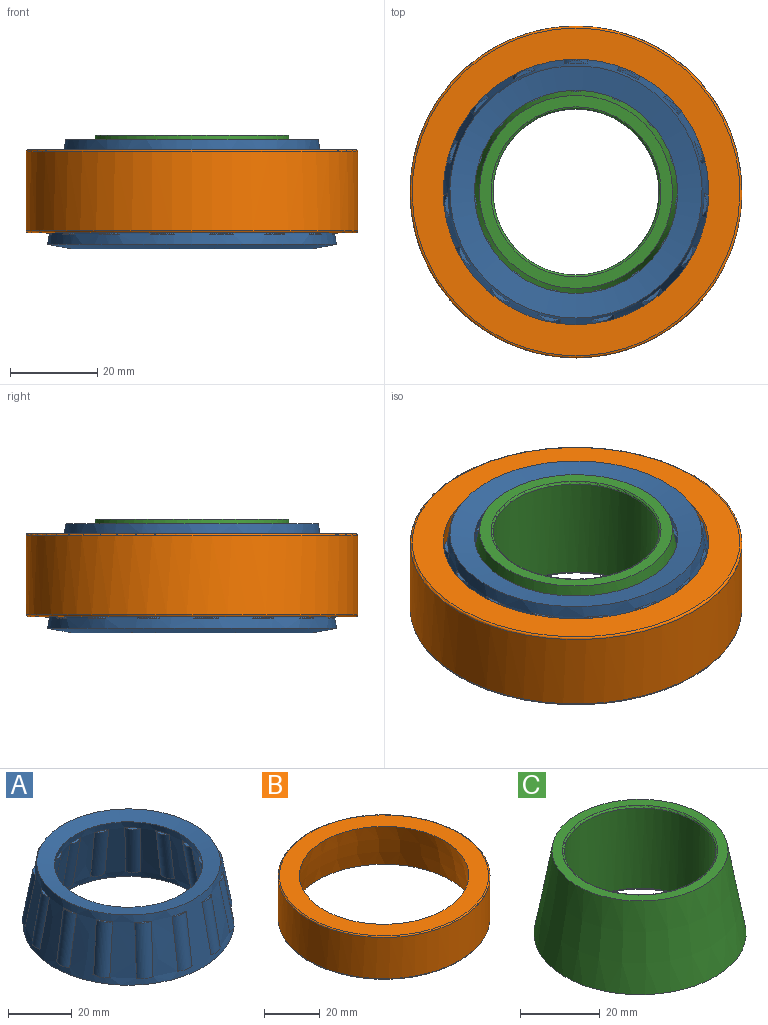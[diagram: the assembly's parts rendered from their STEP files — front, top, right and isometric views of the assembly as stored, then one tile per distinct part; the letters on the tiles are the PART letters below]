
ASSEMBLY  parts=3 mates=3
PART A: 169 faces, bbox 66.9x66.8x25.1 mm
  f0: plane 4.3x1.24mm, normal (0.04,0.17,0.98), area 2.5mm2, adj f2,f123
  f1: plane 4.33x1.25mm, normal (-0.04,-0.17,-0.98), area 2.5mm2, adj f2,f123
  f2: cylinder r=3.69mm len=20.33mm, axis (0.04,0.17,0.98), area 448.5mm2, adj f0,f1,f3,f4,f5,f6,f7,f148
  f3: plane 4.79x1.48mm, normal (0.04,0.17,0.98), area 2.8mm2, adj f2,f122
  f4: plane 4.76x1.47mm, normal (-0.04,-0.17,-0.98), area 2.8mm2, adj f2,f122
  f5: plane 5.52x2.27mm, normal (-0.04,-0.17,-0.98), area 0.8mm2, adj f2,f122,f123,f150
  f6: plane 5.52x2.25mm, normal (0.04,0.17,0.98), area 0.8mm2, adj f2,f122,f123,f150
  f7: plane 5.59x2mm, normal (0.04,0.17,0.98), area 0.8mm2, adj f2,f122,f123,f149
  f8: plane 3.56x2.59mm, normal (0.1,0.14,0.98), area 2.5mm2, adj f10,f123
  f9: plane 3.58x2.6mm, normal (-0.1,-0.14,-0.98), area 2.5mm2, adj f10,f123
  f10: cylinder r=3.69mm len=20.33mm, axis (0.1,0.14,0.98), area 448.5mm2, adj f8,f9,f11,f12,f13,f14,f15,f151
  f11: plane 3.96x2.89mm, normal (0.1,0.14,0.98), area 2.8mm2, adj f10,f122
  f12: plane 3.94x2.87mm, normal (-0.1,-0.14,-0.98), area 2.8mm2, adj f10,f122
  f13: plane 4.54x3.73mm, normal (-0.1,-0.14,-0.98), area 0.8mm2, adj f10,f122,f123,f153
  f14: plane 4.55x3.71mm, normal (0.1,0.14,0.98), area 0.8mm2, adj f10,f122,f123,f153
  f15: plane 4.8x3.43mm, normal (0.1,0.14,0.98), area 0.8mm2, adj f10,f122,f123,f152
  f16: plane 4.37x0.96mm, normal (0.17,0.02,0.98), area 2.5mm2, adj f18,f123
  f17: plane 4.4x0.98mm, normal (-0.17,-0.02,-0.98), area 2.5mm2, adj f18,f123
  f18: cylinder r=3.69mm len=20.33mm, axis (0.17,0.02,0.98), area 448.5mm2, adj f16,f17,f19,f20,f21,f22,f23,f157
  f19: plane 4.87x1.18mm, normal (0.17,0.02,0.98), area 2.8mm2, adj f18,f122
  f20: plane 4.84x1.17mm, normal (-0.17,-0.02,-0.98), area 2.8mm2, adj f18,f122
  f21: plane 5.64x1.67mm, normal (-0.17,-0.02,-0.98), area 0.8mm2, adj f18,f122,f123,f159
  f22: plane 5.64x1.68mm, normal (0.17,0.02,0.98), area 0.8mm2, adj f18,f122,f123,f159
  f23: plane 5.62x1.92mm, normal (0.17,0.02,0.98), area 0.8mm2, adj f18,f122,f123,f158
  f24: plane 4.41x0.82mm, normal (0,-0.17,0.98), area 2.5mm2, adj f26,f123
  f25: plane 4.44x0.82mm, normal (0,0.17,-0.98), area 2.5mm2, adj f26,f123
  f26: cylinder r=3.69mm len=20.33mm, axis (0,-0.17,0.98), area 448.5mm2, adj f24,f25,f27,f28,f29,f30,f31,f124
  f27: plane 4.9x0.92mm, normal (0,-0.17,0.98), area 2.8mm2, adj f26,f122
  f28: plane 4.87x0.91mm, normal (0,0.17,-0.98), area 2.8mm2, adj f26,f122
  f29: plane 5.66x1.62mm, normal (0,0.17,-0.98), area 0.8mm2, adj f26,f122,f123,f126
  f30: plane 5.65x1.6mm, normal (0,-0.17,0.98), area 0.8mm2, adj f26,f122,f123,f126
  f31: plane 5.65x1.6mm, normal (0,-0.17,0.98), area 0.8mm2, adj f26,f122,f123,f125
  f32: plane 4.3x1.24mm, normal (-0.04,0.17,0.98), area 2.5mm2, adj f34,f123
  f33: plane 4.33x1.25mm, normal (0.04,-0.17,-0.98), area 2.5mm2, adj f34,f123
  f34: cylinder r=3.69mm len=20.33mm, axis (-0.04,0.17,0.98), area 448.5mm2, adj f32,f33,f35,f36,f37,f38,f39,f145
  f35: plane 4.79x1.48mm, normal (-0.04,0.17,0.98), area 2.8mm2, adj f34,f122
  f36: plane 4.76x1.47mm, normal (0.04,-0.17,-0.98), area 2.8mm2, adj f34,f122
  f37: plane 5.59x1.99mm, normal (0.04,-0.17,-0.98), area 0.8mm2, adj f34,f122,f123,f147
  f38: plane 5.59x2mm, normal (-0.04,0.17,0.98), area 0.8mm2, adj f34,f122,f123,f147
  f39: plane 5.52x2.25mm, normal (-0.04,0.17,0.98), area 0.8mm2, adj f34,f122,f123,f146
  f40: plane 4.37x0.96mm, normal (-0.17,0.02,0.98), area 2.5mm2, adj f42,f123
  f41: plane 4.4x0.98mm, normal (0.17,-0.02,-0.98), area 2.5mm2, adj f42,f123
  f42: cylinder r=3.69mm len=20.33mm, axis (-0.17,0.02,0.98), area 448.5mm2, adj f40,f41,f43,f44,f45,f46,f47,f136
  f43: plane 4.87x1.18mm, normal (-0.17,0.02,0.98), area 2.8mm2, adj f42,f122
  f44: plane 4.84x1.17mm, normal (0.17,-0.02,-0.98), area 2.8mm2, adj f42,f122
  f45: plane 5.62x1.93mm, normal (0.17,-0.02,-0.98), area 0.8mm2, adj f42,f122,f123,f138
  f46: plane 5.62x1.92mm, normal (-0.17,0.02,0.98), area 0.8mm2, adj f42,f122,f123,f138
  f47: plane 5.64x1.68mm, normal (-0.17,0.02,0.98), area 0.8mm2, adj f42,f122,f123,f137
  f48: plane 3.27x2.94mm, normal (-0.13,-0.12,0.98), area 2.5mm2, adj f50,f123
  f49: plane 3.29x2.96mm, normal (0.13,0.12,-0.98), area 2.5mm2, adj f50,f123
  f50: cylinder r=3.69mm len=20.33mm, axis (-0.13,-0.12,0.98), area 448.5mm2, adj f48,f49,f51,f52,f53,f54,f55,f130
  f51: plane 3.64x3.27mm, normal (-0.13,-0.12,0.98), area 2.8mm2, adj f50,f122
  f52: plane 3.62x3.26mm, normal (0.13,0.12,-0.98), area 2.8mm2, adj f50,f122
  f53: plane 4.48x3.79mm, normal (0.13,0.12,-0.98), area 0.8mm2, adj f50,f122,f123,f131
  f54: plane 4.46x3.81mm, normal (-0.13,-0.12,0.98), area 0.8mm2, adj f50,f122,f123,f131
  f55: plane 4.19x4.09mm, normal (-0.13,-0.12,0.98), area 0.8mm2, adj f50,f122,f123,f132
  f56: plane 3.81x2.22mm, normal (0.15,0.09,0.98), area 2.5mm2, adj f58,f123
  f57: plane 3.84x2.24mm, normal (-0.15,-0.09,-0.98), area 2.5mm2, adj f58,f123
  f58: cylinder r=3.69mm len=20.33mm, axis (0.15,0.09,0.98), area 448.5mm2, adj f56,f57,f59,f60,f61,f62,f63,f154
  f59: plane 4.24x2.52mm, normal (0.15,0.09,0.98), area 2.8mm2, adj f58,f122
  f60: plane 4.22x2.5mm, normal (-0.15,-0.09,-0.98), area 2.8mm2, adj f58,f122
  f61: plane 5.09x3.04mm, normal (-0.15,-0.09,-0.98), area 0.8mm2, adj f58,f122,f123,f155
  f62: plane 5.08x3.06mm, normal (0.15,0.09,0.98), area 0.8mm2, adj f58,f122,f123,f155
  f63: plane 4.88x3.34mm, normal (0.15,0.09,0.98), area 0.8mm2, adj f58,f122,f123,f156
  f64: plane 4.02x1.87mm, normal (0.07,-0.16,0.98), area 2.5mm2, adj f66,f123
  f65: plane 4.05x1.89mm, normal (-0.07,0.16,-0.98), area 2.5mm2, adj f66,f123
  f66: cylinder r=3.69mm len=20.33mm, axis (0.07,-0.16,0.98), area 448.5mm2, adj f64,f65,f67,f68,f69,f70,f71,f166
  f67: plane 4.47x2.15mm, normal (0.07,-0.16,0.98), area 2.8mm2, adj f66,f122
  f68: plane 4.45x2.14mm, normal (-0.07,0.16,-0.98), area 2.8mm2, adj f66,f122
  f69: plane 5.32x2.68mm, normal (-0.07,0.16,-0.98), area 0.8mm2, adj f66,f122,f123,f167
  f70: plane 5.31x2.7mm, normal (0.07,-0.16,0.98), area 0.8mm2, adj f66,f122,f123,f167
  f71: plane 5.15x2.97mm, normal (0.07,-0.16,0.98), area 0.8mm2, adj f66,f122,f123,f168
  f72: plane 4.02x1.87mm, normal (-0.07,-0.16,0.98), area 2.5mm2, adj f74,f123
  f73: plane 4.05x1.89mm, normal (0.07,0.16,-0.98), area 2.5mm2, adj f74,f123
  f74: cylinder r=3.69mm len=20.33mm, axis (-0.07,-0.16,0.98), area 448.5mm2, adj f72,f73,f75,f76,f77,f78,f79,f127
  f75: plane 4.47x2.15mm, normal (-0.07,-0.16,0.98), area 2.8mm2, adj f74,f122
  f76: plane 4.45x2.14mm, normal (0.07,0.16,-0.98), area 2.8mm2, adj f74,f122
  f77: plane 5.14x2.99mm, normal (0.07,0.16,-0.98), area 0.8mm2, adj f74,f122,f123,f129
  f78: plane 5.15x2.97mm, normal (-0.07,-0.16,0.98), area 0.8mm2, adj f74,f122,f123,f129
  f79: plane 5.31x2.7mm, normal (-0.07,-0.16,0.98), area 0.8mm2, adj f74,f122,f123,f128
  f80: plane 4.18x1.54mm, normal (0.17,-0.05,0.98), area 2.5mm2, adj f82,f123
  f81: plane 4.21x1.56mm, normal (-0.17,0.05,-0.98), area 2.5mm2, adj f82,f123
  f82: cylinder r=3.69mm len=20.33mm, axis (0.17,-0.05,0.98), area 448.5mm2, adj f80,f81,f83,f84,f85,f86,f87,f160
  f83: plane 4.65x1.81mm, normal (0.17,-0.05,0.98), area 2.8mm2, adj f82,f122
  f84: plane 4.63x1.79mm, normal (-0.17,0.05,-0.98), area 2.8mm2, adj f82,f122
  f85: plane 5.36x2.62mm, normal (-0.17,0.05,-0.98), area 0.8mm2, adj f82,f122,f123,f162
  f86: plane 5.37x2.6mm, normal (0.17,-0.05,0.98), area 0.8mm2, adj f82,f122,f123,f162
  f87: plane 5.48x2.34mm, normal (0.17,-0.05,0.98), area 0.8mm2, adj f82,f122,f123,f161
  f88: plane 4.18x1.54mm, normal (-0.17,-0.05,0.98), area 2.5mm2, adj f90,f123
  f89: plane 4.21x1.56mm, normal (0.17,0.05,-0.98), area 2.5mm2, adj f90,f123
  f90: cylinder r=3.69mm len=20.33mm, axis (-0.17,-0.05,0.98), area 448.5mm2, adj f88,f89,f91,f92,f93,f94,f95,f133
  f91: plane 4.65x1.81mm, normal (-0.17,-0.05,0.98), area 2.8mm2, adj f90,f122
  f92: plane 4.63x1.79mm, normal (0.17,0.05,-0.98), area 2.8mm2, adj f90,f122
  f93: plane 5.49x2.33mm, normal (0.17,0.05,-0.98), area 0.8mm2, adj f90,f122,f123,f135
  f94: plane 5.48x2.34mm, normal (-0.17,-0.05,0.98), area 0.8mm2, adj f90,f122,f123,f135
  f95: plane 5.37x2.6mm, normal (-0.17,-0.05,0.98), area 0.8mm2, adj f90,f122,f123,f134
  f96: plane 3.56x2.59mm, normal (-0.1,0.14,0.98), area 2.5mm2, adj f98,f123
  f97: plane 3.58x2.6mm, normal (0.1,-0.14,-0.98), area 2.5mm2, adj f98,f123
  f98: cylinder r=3.69mm len=20.33mm, axis (-0.1,0.14,0.98), area 448.5mm2, adj f96,f97,f99,f100,f101,f102,f103,f142
  f99: plane 3.96x2.89mm, normal (-0.1,0.14,0.98), area 2.8mm2, adj f98,f122
  f100: plane 3.94x2.87mm, normal (0.1,-0.14,-0.98), area 2.8mm2, adj f98,f122
  f101: plane 4.81x3.42mm, normal (0.1,-0.14,-0.98), area 0.8mm2, adj f98,f122,f123,f143
  f102: plane 4.8x3.43mm, normal (-0.1,0.14,0.98), area 0.8mm2, adj f98,f122,f123,f143
  f103: plane 4.55x3.71mm, normal (-0.1,0.14,0.98), area 0.8mm2, adj f98,f122,f123,f144
  f104: plane 3.27x2.94mm, normal (0.13,-0.12,0.98), area 2.5mm2, adj f106,f123
  f105: plane 3.29x2.96mm, normal (-0.13,0.12,-0.98), area 2.5mm2, adj f106,f123
  f106: cylinder r=3.69mm len=20.33mm, axis (0.13,-0.12,0.98), area 448.5mm2, adj f104,f105,f107,f108,f109,f110,f111,f163
  f107: plane 3.64x3.27mm, normal (0.13,-0.12,0.98), area 2.8mm2, adj f106,f122
  f108: plane 3.62x3.26mm, normal (-0.13,0.12,-0.98), area 2.8mm2, adj f106,f122
  f109: plane 4.17x4.11mm, normal (-0.13,0.12,-0.98), area 0.8mm2, adj f106,f122,f123,f164
  f110: plane 4.19x4.09mm, normal (0.13,-0.12,0.98), area 0.8mm2, adj f106,f122,f123,f164
  f111: plane 4.46x3.81mm, normal (0.13,-0.12,0.98), area 0.8mm2, adj f106,f122,f123,f165
  f112: plane 3.81x2.22mm, normal (-0.15,0.09,0.98), area 2.5mm2, adj f114,f123
  f113: plane 3.84x2.24mm, normal (0.15,-0.09,-0.98), area 2.5mm2, adj f114,f123
  f114: cylinder r=3.69mm len=20.33mm, axis (-0.15,0.09,0.98), area 448.5mm2, adj f112,f113,f115,f116,f117,f118,f119,f139
  f115: plane 4.24x2.52mm, normal (-0.15,0.09,0.98), area 2.8mm2, adj f114,f122
  f116: plane 4.22x2.5mm, normal (0.15,-0.09,-0.98), area 2.8mm2, adj f114,f122
  f117: plane 4.87x3.36mm, normal (0.15,-0.09,-0.98), area 0.8mm2, adj f114,f122,f123,f141
  f118: plane 4.88x3.34mm, normal (-0.15,0.09,0.98), area 0.8mm2, adj f114,f122,f123,f141
  f119: plane 5.08x3.06mm, normal (-0.15,0.09,0.98), area 0.8mm2, adj f114,f122,f123,f140
  f120: cone r=27.56mm half-angle=80deg, axis (0,0,1), area 1093mm2, adj f122,f123
  f121: cone r=28.96mm half-angle=80deg, axis (0,0,1), area 940.3mm2, adj f122,f123
  f122: cone r=33.2mm half-angle=10deg, axis (0,0,-1), area 3233.8mm2, adj f3,f4,f5,f6,f7,f11,f12,f13
  f123: cone r=27.06mm half-angle=10deg, axis (0,0,-1), area 2513.7mm2, adj f0,f1,f5,f6,f7,f8,f9,f13
  f124: plane 5.66x1.62mm, normal (0,0.17,-0.98), area 0.8mm2, adj f26,f122,f123,f125
  f125: cylinder r=3.82mm len=20.05mm, axis (0,-0.17,0.98), area 125.4mm2, adj f31,f122,f123,f124
  f126: cylinder r=3.82mm len=20.05mm, axis (0,-0.17,0.98), area 125.4mm2, adj f29,f30,f122,f123
  f127: plane 5.32x2.68mm, normal (0.07,0.16,-0.98), area 0.8mm2, adj f74,f122,f123,f128
  f128: cylinder r=3.82mm len=20.05mm, axis (-0.07,-0.16,0.98), area 125.4mm2, adj f79,f122,f123,f127
  f129: cylinder r=3.82mm len=20.05mm, axis (-0.07,-0.16,0.98), area 125.4mm2, adj f77,f78,f122,f123
  f130: plane 4.17x4.11mm, normal (0.13,0.12,-0.98), area 0.8mm2, adj f50,f122,f123,f132
  f131: cylinder r=3.82mm len=20.05mm, axis (-0.13,-0.12,0.98), area 125.4mm2, adj f53,f54,f122,f123
  f132: cylinder r=3.82mm len=20.05mm, axis (-0.13,-0.12,0.98), area 125.4mm2, adj f55,f122,f123,f130
  f133: plane 5.36x2.62mm, normal (0.17,0.05,-0.98), area 0.8mm2, adj f90,f122,f123,f134
  f134: cylinder r=3.82mm len=20.05mm, axis (-0.17,-0.05,0.98), area 125.4mm2, adj f95,f122,f123,f133
  f135: cylinder r=3.82mm len=20.05mm, axis (-0.17,-0.05,0.98), area 125.4mm2, adj f93,f94,f122,f123
  f136: plane 5.64x1.67mm, normal (0.17,-0.02,-0.98), area 0.8mm2, adj f42,f122,f123,f137
  f137: cylinder r=3.82mm len=20.05mm, axis (-0.17,0.02,0.98), area 125.4mm2, adj f47,f122,f123,f136
  f138: cylinder r=3.82mm len=20.05mm, axis (-0.17,0.02,0.98), area 125.4mm2, adj f45,f46,f122,f123
  f139: plane 5.09x3.04mm, normal (0.15,-0.09,-0.98), area 0.8mm2, adj f114,f122,f123,f140
  f140: cylinder r=3.82mm len=20.05mm, axis (-0.15,0.09,0.98), area 125.4mm2, adj f119,f122,f123,f139
  f141: cylinder r=3.82mm len=20.05mm, axis (-0.15,0.09,0.98), area 125.4mm2, adj f117,f118,f122,f123
  f142: plane 4.54x3.73mm, normal (0.1,-0.14,-0.98), area 0.8mm2, adj f98,f122,f123,f144
  f143: cylinder r=3.82mm len=20.05mm, axis (-0.1,0.14,0.98), area 125.4mm2, adj f101,f102,f122,f123
  f144: cylinder r=3.82mm len=20.05mm, axis (-0.1,0.14,0.98), area 125.4mm2, adj f103,f122,f123,f142
  f145: plane 5.52x2.27mm, normal (0.04,-0.17,-0.98), area 0.8mm2, adj f34,f122,f123,f146
  f146: cylinder r=3.82mm len=20.05mm, axis (-0.04,0.17,0.98), area 125.4mm2, adj f39,f122,f123,f145
  f147: cylinder r=3.82mm len=20.05mm, axis (-0.04,0.17,0.98), area 125.4mm2, adj f37,f38,f122,f123
  f148: plane 5.59x1.99mm, normal (-0.04,-0.17,-0.98), area 0.8mm2, adj f2,f122,f123,f149
  f149: cylinder r=3.82mm len=20.05mm, axis (0.04,0.17,0.98), area 125.4mm2, adj f7,f122,f123,f148
  f150: cylinder r=3.82mm len=20.05mm, axis (0.04,0.17,0.98), area 125.4mm2, adj f5,f6,f122,f123
  f151: plane 4.81x3.42mm, normal (-0.1,-0.14,-0.98), area 0.8mm2, adj f10,f122,f123,f152
  f152: cylinder r=3.82mm len=20.05mm, axis (0.1,0.14,0.98), area 125.4mm2, adj f15,f122,f123,f151
  f153: cylinder r=3.82mm len=20.05mm, axis (0.1,0.14,0.98), area 125.4mm2, adj f13,f14,f122,f123
  f154: plane 4.87x3.36mm, normal (-0.15,-0.09,-0.98), area 0.8mm2, adj f58,f122,f123,f156
  f155: cylinder r=3.82mm len=20.05mm, axis (0.15,0.09,0.98), area 125.4mm2, adj f61,f62,f122,f123
  f156: cylinder r=3.82mm len=20.05mm, axis (0.15,0.09,0.98), area 125.4mm2, adj f63,f122,f123,f154
  f157: plane 5.62x1.93mm, normal (-0.17,-0.02,-0.98), area 0.8mm2, adj f18,f122,f123,f158
  f158: cylinder r=3.82mm len=20.05mm, axis (0.17,0.02,0.98), area 125.4mm2, adj f23,f122,f123,f157
  f159: cylinder r=3.82mm len=20.05mm, axis (0.17,0.02,0.98), area 125.4mm2, adj f21,f22,f122,f123
  f160: plane 5.49x2.33mm, normal (-0.17,0.05,-0.98), area 0.8mm2, adj f82,f122,f123,f161
  f161: cylinder r=3.82mm len=20.05mm, axis (0.17,-0.05,0.98), area 125.4mm2, adj f87,f122,f123,f160
  f162: cylinder r=3.82mm len=20.05mm, axis (0.17,-0.05,0.98), area 125.4mm2, adj f85,f86,f122,f123
  f163: plane 4.48x3.79mm, normal (-0.13,0.12,-0.98), area 0.8mm2, adj f106,f122,f123,f165
  f164: cylinder r=3.82mm len=20.05mm, axis (0.13,-0.12,0.98), area 125.4mm2, adj f109,f110,f122,f123
  f165: cylinder r=3.82mm len=20.05mm, axis (0.13,-0.12,0.98), area 125.4mm2, adj f111,f122,f123,f163
  f166: plane 5.14x2.99mm, normal (-0.07,0.16,-0.98), area 0.8mm2, adj f66,f122,f123,f168
  f167: cylinder r=3.82mm len=20.05mm, axis (0.07,-0.16,0.98), area 125.4mm2, adj f69,f70,f122,f123
  f168: cylinder r=3.82mm len=20.05mm, axis (0.07,-0.16,0.98), area 125.4mm2, adj f71,f122,f123,f166
PART B: 6 faces, bbox 82.5x82.5x19.1 mm
  f0: torus R=37.62mm, axis (0,0,-1), area 178.3mm2, adj f3,f4
  f1: torus R=37.62mm, axis (0,0,1), area 178.3mm2, adj f3,f5
  f2: cone r=30.48mm half-angle=10deg, axis (0,0,-1), area 3908.7mm2, adj f4,f5
  f3: cylinder r=38.1mm len=76.2mm, axis (0,0,1), area 4332.3mm2, adj f0,f1
  f4: plane 75.25x75.25mm, normal (0,0,1), area 1528.4mm2, adj f0,f2
  f5: plane 75.25x75.25mm, normal (0,0,-1), area 849.7mm2, adj f1,f2
PART C: 6 faces, bbox 53.3x53.3x25.7 mm
  f0: torus R=19.53mm, axis (0,0,-1), area 90.4mm2, adj f3,f5
  f1: torus R=19.53mm, axis (0,0,1), area 90.4mm2, adj f3,f4
  f2: cone r=26.67mm half-angle=10deg, axis (0,0,-1), area 3995mm2, adj f4,f5
  f3: cylinder r=19.05mm len=38.1mm, axis (0,0,1), area 2956.6mm2, adj f0,f1
  f4: plane 53.34x53.34mm, normal (0,0,-1), area 1036.8mm2, adj f1,f2
  f5: plane 44.29x44.29mm, normal (0,0,1), area 343mm2, adj f0,f2
PLACE A t=(-18.92,-10.11,1.21)mm
PLACE B t=(-18.92,-10.11,2.04)mm
PLACE C t=(-18.92,-10.11,2.04)mm
MATE fastened C.f3 <-> B.f2  axis (0,0,-1) through (-18.92,-10.11,14.86)mm
MATE fastened C.f0 <-> B.f0  axis (0,0,-1) through (-18.92,-10.11,-10.79)mm
MATE fastened C.f2 <-> A.f121  axis (0,0,1) through (-18.92,-10.11,14.86)mm
